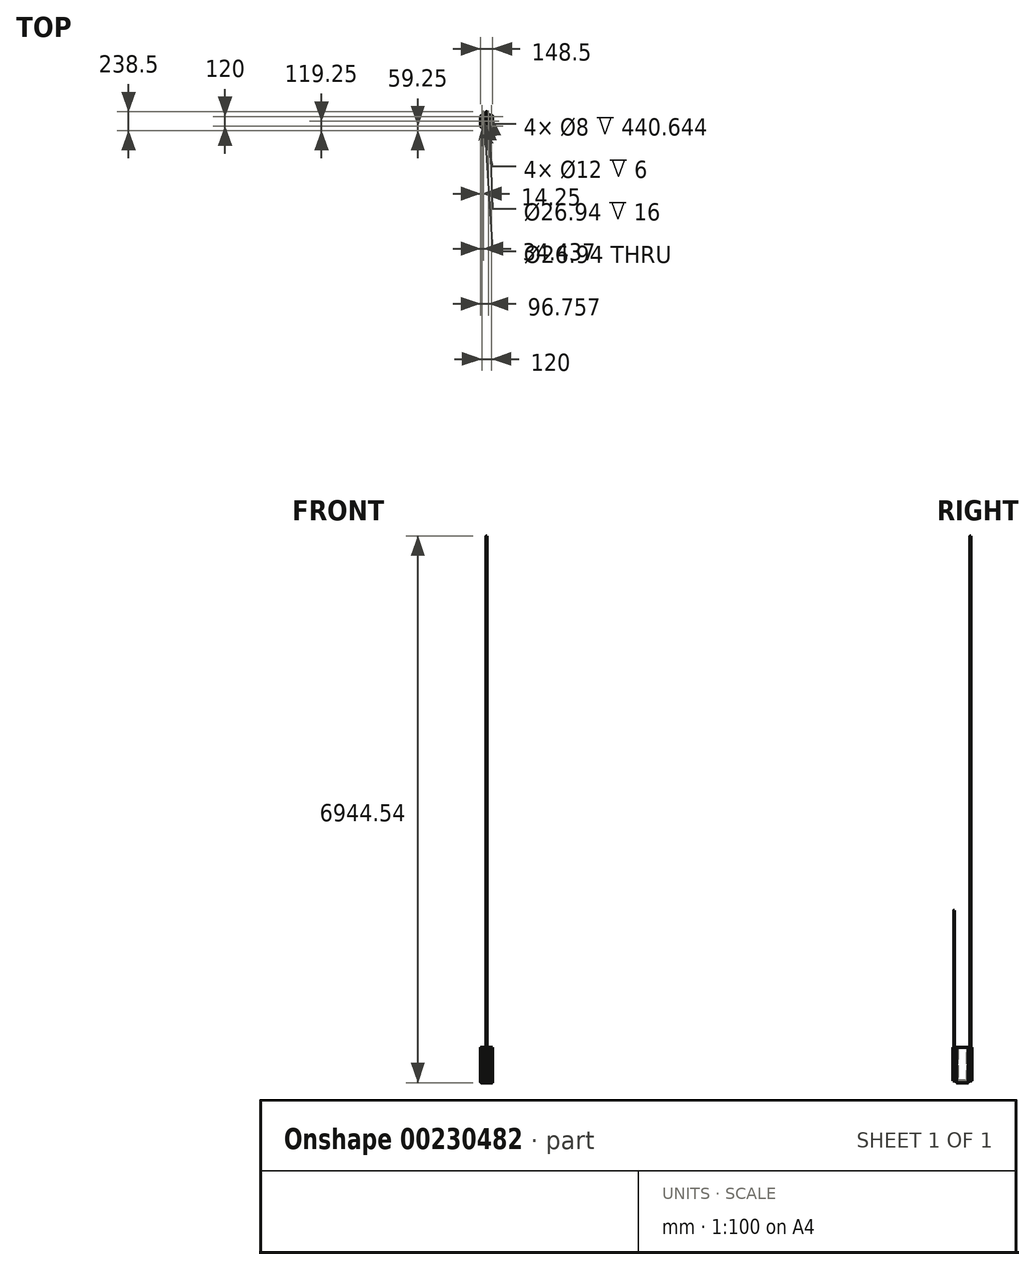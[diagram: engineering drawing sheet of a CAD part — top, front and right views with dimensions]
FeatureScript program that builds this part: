
annotation { "Feature Type Name" : "Feature", "Feature Type Description" : "" }
export const myFeature = defineFeature(function(context is Context, id is Id, definition is map)
    precondition{}
    {
        {
            var Q0;
            Q0=qCreatedBy(makeId("Top.planeOp"),FACE);
            var sketch = newSketch(context, id + "F0", { "sketchPlane" : qUnion([Q0])});
            skPoint(sketch, "E0.rect.middle", {"position": v(0, 0) * mm});
            skLineSegment(sketch, "E1.bottom", {"start": v(-64.25, -74.25) * mm, "end": v(64.25, -74.25) * mm});
            skLineSegment(sketch, "E1.top", {"start": v(-64.25, 74.25) * mm, "end": v(64.25, 74.25) * mm});
            skLineSegment(sketch, "E1.left", {"start": v(-74.25, -64.25) * mm, "end": v(-74.25, 64.25) * mm});
            skLineSegment(sketch, "E1.right", {"start": v(74.25, -64.25) * mm, "end": v(74.25, 64.25) * mm});
            skLineSegment(sketch, "E2", {"start": v(-74.25, 74.25) * mm, "end": v(74.25, -74.25) * mm, "construction": true});
            skLineSegment(sketch, "E3", {"start": v(74.25, 74.25) * mm, "end": v(-74.25, -74.25) * mm, "construction": true});
            skCircle(sketch, "E4", {"center": v(-60, 60) * mm, "radius": 4 * mm});
            skCircle(sketch, "E5", {"center": v(60, 60) * mm, "radius": 4 * mm});
            skCircle(sketch, "E6", {"center": v(60, -60) * mm, "radius": 4 * mm});
            skCircle(sketch, "E7", {"center": v(-60, -60) * mm, "radius": 4 * mm});
            skLineSegment(sketch, "E8", {"start": v(-60, 60) * mm, "end": v(60, 60) * mm, "construction": true});
            skLineSegment(sketch, "E9", {"start": v(60, 60) * mm, "end": v(60, -60) * mm, "construction": true});
            skLineSegment(sketch, "E10", {"start": v(60, -60) * mm, "end": v(-60, -60) * mm, "construction": true});
            skLineSegment(sketch, "E11", {"start": v(-60, -60) * mm, "end": v(-60, 60) * mm, "construction": true});
            skLineSegment(sketch, "E12", {"start": v(-60, 38.83) * mm, "end": v(-60, -38.83) * mm});
            skLineSegment(sketch, "E13", {"start": v(60, 38.83) * mm, "end": v(60, -38.83) * mm});
            skArc(sketch, "E14", {"start": v(54.26, 47.88) * mm, "mid": v(0, 60) * mm, "end": v(-54.26, 47.88) * mm});
            skArc(sketch, "E15", {"start": v(-54.26, -47.88) * mm, "mid": v(0, -60) * mm, "end": v(54.26, -47.88) * mm});
            skLineSegment(sketch, "E16", {"start": v(-60, 0) * mm, "end": v(60, 0) * mm, "construction": true});
            skPoint(sketch, "E17.visualSharp", {"position": v(-60, -45) * mm});
            skArc(sketch, "E17.filletArc", {"start": v(-60, -38.83) * mm, "mid": v(-58.44, -44.2) * mm, "end": v(-54.26, -47.88) * mm});
            skPoint(sketch, "E18.visualSharp", {"position": v(-60, 45) * mm});
            skArc(sketch, "E18.filletArc", {"start": v(-54.26, 47.88) * mm, "mid": v(-58.44, 44.2) * mm, "end": v(-60, 38.83) * mm});
            skPoint(sketch, "E19.visualSharp", {"position": v(60, 45) * mm});
            skArc(sketch, "E19.filletArc", {"start": v(60, 38.83) * mm, "mid": v(58.44, 44.2) * mm, "end": v(54.26, 47.88) * mm});
            skPoint(sketch, "E20.visualSharp", {"position": v(60, -45) * mm});
            skArc(sketch, "E20.filletArc", {"start": v(54.26, -47.88) * mm, "mid": v(58.44, -44.2) * mm, "end": v(60, -38.83) * mm});
            skPoint(sketch, "E21.visualSharp", {"position": v(-74.25, 74.25) * mm});
            skArc(sketch, "E21.filletArc", {"start": v(-64.25, 74.25) * mm, "mid": v(-71.32, 71.32) * mm, "end": v(-74.25, 64.25) * mm});
            skPoint(sketch, "E22.visualSharp", {"position": v(74.25, 74.25) * mm});
            skArc(sketch, "E22.filletArc", {"start": v(74.25, 64.25) * mm, "mid": v(71.32, 71.32) * mm, "end": v(64.25, 74.25) * mm});
            skPoint(sketch, "E23.visualSharp", {"position": v(74.25, -74.25) * mm});
            skArc(sketch, "E23.filletArc", {"start": v(64.25, -74.25) * mm, "mid": v(71.32, -71.32) * mm, "end": v(74.25, -64.25) * mm});
            skPoint(sketch, "E24.visualSharp", {"position": v(-74.25, -74.25) * mm});
            skArc(sketch, "E24.filletArc", {"start": v(-74.25, -64.25) * mm, "mid": v(-71.32, -71.32) * mm, "end": v(-64.25, -74.25) * mm});
            skArc(sketch, "E25.0", {"start": v(57, 38.83) * mm, "mid": v(55.9, 42.58) * mm, "end": v(52.98, 45.17) * mm});
            skLineSegment(sketch, "E25.1", {"start": v(57, 38.83) * mm, "end": v(57, -38.83) * mm});
            skArc(sketch, "E25.2", {"start": v(52.98, -45.17) * mm, "mid": v(55.9, -42.58) * mm, "end": v(57, -38.83) * mm});
            skArc(sketch, "E25.3", {"start": v(-52.98, -45.17) * mm, "mid": v(0, -57) * mm, "end": v(52.98, -45.17) * mm});
            skArc(sketch, "E25.4", {"start": v(-57, -38.83) * mm, "mid": v(-55.9, -42.58) * mm, "end": v(-52.98, -45.17) * mm});
            skArc(sketch, "E25.5", {"start": v(52.98, 45.17) * mm, "mid": v(0, 57) * mm, "end": v(-52.98, 45.17) * mm});
            skLineSegment(sketch, "E25.6", {"start": v(-57, 38.83) * mm, "end": v(-57, -38.83) * mm});
            skArc(sketch, "E25.7", {"start": v(-52.98, 45.17) * mm, "mid": v(-55.9, 42.58) * mm, "end": v(-57, 38.83) * mm});
            skArc(sketch, "E26.0", {"start": v(-55.96, 51.5) * mm, "mid": v(-61.82, 46.33) * mm, "end": v(-64, 38.83) * mm});
            skArc(sketch, "E26.1", {"start": v(55.96, 51.5) * mm, "mid": v(0, 64) * mm, "end": v(-55.96, 51.5) * mm});
            skArc(sketch, "E26.2", {"start": v(64, 38.83) * mm, "mid": v(61.82, 46.33) * mm, "end": v(55.96, 51.5) * mm});
            skLineSegment(sketch, "E26.3", {"start": v(64, 38.83) * mm, "end": v(64, -38.83) * mm});
            skArc(sketch, "E26.4", {"start": v(55.96, -51.5) * mm, "mid": v(61.82, -46.33) * mm, "end": v(64, -38.83) * mm});
            skLineSegment(sketch, "E26.5", {"start": v(-64, 38.83) * mm, "end": v(-64, -38.83) * mm});
            skArc(sketch, "E26.6", {"start": v(-55.96, -51.5) * mm, "mid": v(0, -64) * mm, "end": v(55.96, -51.5) * mm});
            skArc(sketch, "E26.7", {"start": v(-64, -38.83) * mm, "mid": v(-61.82, -46.33) * mm, "end": v(-55.96, -51.5) * mm});
            skSolve(sketch);
        }
        {
            var Q0;
            Q0=makeQuery(id+"F0.imprint","IMPRINT",FACE,{"disambiguationData":[TD([[makeQuery(id+"F0.imprint","IMPRINT",EDGE,{"derivedFrom":sQuery(id+"F0.wireOp",EDGE,"E1.bottom")}),1.0]])]});
            var Q1;
            Q1=makeQuery(id+"F0.imprint","IMPRINT",FACE,{"disambiguationData":[TD([[makeQuery(id+"F0.imprint","IMPRINT",EDGE,{"derivedFrom":sQuery(id+"F0.wireOp",EDGE,"E12")}),1.0]])]});
            var Q2;
            Q2=makeQuery(id+"F0.imprint","IMPRINT",FACE,{"disambiguationData":[TD([[makeQuery(id+"F0.imprint","IMPRINT",EDGE,{"derivedFrom":sQuery(id+"F0.wireOp",EDGE,"E25.0")}),1.0]])]});
            var Q3;
            Q3=makeQuery(id+"F0.imprint","IMPRINT",FACE,{"disambiguationData":[TD([[makeQuery(id+"F0.imprint","IMPRINT",EDGE,{"derivedFrom":sQuery(id+"F0.wireOp",EDGE,"E12")}),-1.0]])]});
            extrude(context, id + "F1", {"entities" : qUnion([Q0, Q1, Q2, Q3]), "oppositeDirection" : true, "depth" : 25 * mm});
        }
        {
            var Q0;
            Q0=makeQuery(id+"F0.imprint","IMPRINT",FACE,{"disambiguationData":[TD([[makeQuery(id+"F0.imprint","IMPRINT",EDGE,{"derivedFrom":sQuery(id+"F0.wireOp",EDGE,"E12")}),1.0]])]});
            extrude(context, id + "F2", {"entities" : qUnion([Q0]), "operationType" : NewBodyOperationType.ADD, "depth" : 3 * mm});
        }
        {
            var Q0;
            Q0=makeQuery(id+"F0.imprint","IMPRINT",FACE,{"disambiguationData":[TD([[makeQuery(id+"F0.imprint","IMPRINT",EDGE,{"derivedFrom":sQuery(id+"F0.wireOp",EDGE,"E25.0")}),1.0]])]});
            extrude(context, id + "F3", {"entities" : qUnion([Q0]), "operationType" : NewBodyOperationType.REMOVE, "oppositeDirection" : true, "depth" : 18 * mm});
        }
        {
            var Q0;
            Q0=makeQuery(id+"F2.opExtrude","CAP_FACE",FACE,{"disambiguationData":[OSD([sQuery(id+"F0.wireOp",EDGE,"E12"),sQuery(id+"F0.wireOp",EDGE,"E13"),sQuery(id+"F0.wireOp",EDGE,"E14"),sQuery(id+"F0.wireOp",EDGE,"E15"),sQuery(id+"F0.wireOp",EDGE,"E17.filletArc"),sQuery(id+"F0.wireOp",EDGE,"E18.filletArc"),sQuery(id+"F0.wireOp",EDGE,"E19.filletArc"),sQuery(id+"F0.wireOp",EDGE,"E20.filletArc"),sQuery(id+"F0.wireOp",EDGE,"E25.0"),sQuery(id+"F0.wireOp",EDGE,"E25.1"),sQuery(id+"F0.wireOp",EDGE,"E25.2"),sQuery(id+"F0.wireOp",EDGE,"E25.3"),sQuery(id+"F0.wireOp",EDGE,"E25.4"),sQuery(id+"F0.wireOp",EDGE,"E25.5"),sQuery(id+"F0.wireOp",EDGE,"E25.6"),sQuery(id+"F0.wireOp",EDGE,"E25.7")])],"isStart":false});
            var sketch = newSketch(context, id + "F4", { "sketchPlane" : qUnion([Q0])});
            skArc(sketch, "E27.0", {"start": v(-18.34, -40.45) * mm, "mid": v(0, -42) * mm, "end": v(18.34, -40.45) * mm});
            skArc(sketch, "E28.0", {"start": v(18.34, 40.45) * mm, "mid": v(0, 42) * mm, "end": v(-18.34, 40.45) * mm});
            skLineSegment(sketch, "E29", {"start": v(-25, 32.57) * mm, "end": v(-25, -32.57) * mm});
            skLineSegment(sketch, "E30", {"start": v(25, 32.57) * mm, "end": v(25, -32.57) * mm});
            skLineSegment(sketch, "E31", {"start": v(-25, 39.1) * mm, "end": v(25, 39.1) * mm, "construction": true});
            skLineSegment(sketch, "E32", {"start": v(-25, -39.1) * mm, "end": v(25, -39.1) * mm, "construction": true});
            skPoint(sketch, "E33.visualSharp", {"position": v(-25, 39.1) * mm});
            skArc(sketch, "E33.filletArc", {"start": v(-18.34, 40.45) * mm, "mid": v(-23.11, 37.73) * mm, "end": v(-25, 32.57) * mm});
            skPoint(sketch, "E34.visualSharp", {"position": v(25, 39.1) * mm});
            skArc(sketch, "E34.filletArc", {"start": v(25, 32.57) * mm, "mid": v(23.11, 37.73) * mm, "end": v(18.34, 40.45) * mm});
            skPoint(sketch, "E35.visualSharp", {"position": v(25, -39.1) * mm});
            skArc(sketch, "E35.filletArc", {"start": v(18.34, -40.45) * mm, "mid": v(23.11, -37.73) * mm, "end": v(25, -32.57) * mm});
            skPoint(sketch, "E36.visualSharp", {"position": v(-25, -39.1) * mm});
            skArc(sketch, "E36.filletArc", {"start": v(-25, -32.57) * mm, "mid": v(-23.11, -37.73) * mm, "end": v(-18.34, -40.45) * mm});
            skArc(sketch, "E37.0", {"start": v(52.98, 45.17) * mm, "mid": v(0, 57) * mm, "end": v(-52.98, 45.17) * mm});
            skArc(sketch, "E37.1", {"start": v(-52.98, 45.17) * mm, "mid": v(-55.9, 42.58) * mm, "end": v(-57, 38.83) * mm});
            skLineSegment(sketch, "E37.2", {"start": v(-57, 38.83) * mm, "end": v(-57, -38.83) * mm});
            skArc(sketch, "E37.3", {"start": v(-57, -38.83) * mm, "mid": v(-55.9, -42.58) * mm, "end": v(-52.98, -45.17) * mm});
            skArc(sketch, "E37.4", {"start": v(-52.98, -45.17) * mm, "mid": v(0, -57) * mm, "end": v(52.98, -45.17) * mm});
            skArc(sketch, "E37.5", {"start": v(52.98, -45.17) * mm, "mid": v(55.9, -42.58) * mm, "end": v(57, -38.83) * mm});
            skLineSegment(sketch, "E37.6", {"start": v(57, 38.83) * mm, "end": v(57, -38.83) * mm});
            skArc(sketch, "E37.7", {"start": v(57, 38.83) * mm, "mid": v(55.9, 42.58) * mm, "end": v(52.98, 45.17) * mm});
            skLineSegment(sketch, "E38.0", {"start": v(23, 32.57) * mm, "end": v(23, -32.57) * mm});
            skArc(sketch, "E38.1", {"start": v(18, -38.48) * mm, "mid": v(21.58, -36.44) * mm, "end": v(23, -32.57) * mm});
            skArc(sketch, "E38.2", {"start": v(-18, -38.48) * mm, "mid": v(0, -40) * mm, "end": v(18, -38.48) * mm});
            skArc(sketch, "E38.3", {"start": v(-23, -32.57) * mm, "mid": v(-21.58, -36.44) * mm, "end": v(-18, -38.48) * mm});
            skLineSegment(sketch, "E38.4", {"start": v(-23, 32.57) * mm, "end": v(-23, -32.57) * mm});
            skArc(sketch, "E38.5", {"start": v(23, 32.57) * mm, "mid": v(21.58, 36.44) * mm, "end": v(18, 38.48) * mm});
            skArc(sketch, "E38.6", {"start": v(-18, 38.48) * mm, "mid": v(-21.58, 36.44) * mm, "end": v(-23, 32.57) * mm});
            skArc(sketch, "E38.7", {"start": v(18, 38.48) * mm, "mid": v(0, 40) * mm, "end": v(-18, 38.48) * mm});
            skArc(sketch, "E39.0", {"start": v(21, 32.57) * mm, "mid": v(20.06, 35.15) * mm, "end": v(17.67, 36.5) * mm});
            skLineSegment(sketch, "E39.1", {"start": v(21, 32.57) * mm, "end": v(21, -32.57) * mm});
            skArc(sketch, "E39.2", {"start": v(17.67, -36.5) * mm, "mid": v(20.06, -35.15) * mm, "end": v(21, -32.57) * mm});
            skArc(sketch, "E39.3", {"start": v(-17.67, -36.5) * mm, "mid": v(0, -38) * mm, "end": v(17.67, -36.5) * mm});
            skArc(sketch, "E39.4", {"start": v(-21, -32.57) * mm, "mid": v(-20.06, -35.15) * mm, "end": v(-17.67, -36.5) * mm});
            skArc(sketch, "E39.5", {"start": v(17.67, 36.5) * mm, "mid": v(0, 38) * mm, "end": v(-17.67, 36.5) * mm});
            skLineSegment(sketch, "E39.6", {"start": v(-21, 32.57) * mm, "end": v(-21, -32.57) * mm});
            skArc(sketch, "E39.7", {"start": v(-17.67, 36.5) * mm, "mid": v(-20.06, 35.15) * mm, "end": v(-21, 32.57) * mm});
            skLineSegment(sketch, "E40", {"start": v(-25, 0) * mm, "end": v(25, 0) * mm, "construction": true});
            skLineSegment(sketch, "E41", {"start": v(-11, 5.5) * mm, "end": v(-11, 27.5) * mm});
            skLineSegment(sketch, "E42", {"start": v(-8, 30.5) * mm, "end": v(8, 30.5) * mm});
            skLineSegment(sketch, "E43", {"start": v(11, 27.5) * mm, "end": v(11, 13.5) * mm});
            skLineSegment(sketch, "E44", {"start": v(14, 10.5) * mm, "end": v(14, 10.5) * mm});
            skLineSegment(sketch, "E45", {"start": v(17, 7.5) * mm, "end": v(17, 5.5) * mm});
            skLineSegment(sketch, "E46", {"start": v(14, 2.5) * mm, "end": v(-8, 2.5) * mm});
            skPoint(sketch, "E47.visualSharp", {"position": v(-11, 30.5) * mm});
            skArc(sketch, "E47.filletArc", {"start": v(-8, 30.5) * mm, "mid": v(-10.12, 29.62) * mm, "end": v(-11, 27.5) * mm});
            skPoint(sketch, "E48.visualSharp", {"position": v(11, 30.5) * mm});
            skArc(sketch, "E48.filletArc", {"start": v(11, 27.5) * mm, "mid": v(10.12, 29.62) * mm, "end": v(8, 30.5) * mm});
            skPoint(sketch, "E49.visualSharp", {"position": v(11, 10.5) * mm});
            skArc(sketch, "E49.filletArc", {"start": v(11, 13.5) * mm, "mid": v(11.88, 11.38) * mm, "end": v(14, 10.5) * mm});
            skPoint(sketch, "E50.visualSharp", {"position": v(17, 10.5) * mm});
            skArc(sketch, "E50.filletArc", {"start": v(17, 7.5) * mm, "mid": v(16.12, 9.62) * mm, "end": v(14, 10.5) * mm});
            skPoint(sketch, "E51.visualSharp", {"position": v(17, 2.5) * mm});
            skArc(sketch, "E51.filletArc", {"start": v(14, 2.5) * mm, "mid": v(16.12, 3.38) * mm, "end": v(17, 5.5) * mm});
            skPoint(sketch, "E52.visualSharp", {"position": v(-11, 2.5) * mm});
            skArc(sketch, "E52.filletArc", {"start": v(-11, 5.5) * mm, "mid": v(-10.12, 3.38) * mm, "end": v(-8, 2.5) * mm});
            skLineSegment(sketch, "E53.0.MirrorCS", {"start": v(14, -2.5) * mm, "end": v(-8, -2.5) * mm});
            skArc(sketch, "E54.0.MirrorCS", {"start": v(-11, -5.5) * mm, "mid": v(-10.12, -3.38) * mm, "end": v(-8, -2.5) * mm});
            skLineSegment(sketch, "E55.0.MirrorCS", {"start": v(-11, -5.5) * mm, "end": v(-11, -27.5) * mm});
            skArc(sketch, "E56.0.MirrorCS", {"start": v(-8, -30.5) * mm, "mid": v(-10.12, -29.62) * mm, "end": v(-11, -27.5) * mm});
            skLineSegment(sketch, "E57.0.MirrorCS", {"start": v(-8, -30.5) * mm, "end": v(8, -30.5) * mm});
            skArc(sketch, "E58.0.MirrorCS", {"start": v(11, -27.5) * mm, "mid": v(10.12, -29.62) * mm, "end": v(8, -30.5) * mm});
            skLineSegment(sketch, "E59.0.MirrorCS", {"start": v(11, -27.5) * mm, "end": v(11, -13.5) * mm});
            skArc(sketch, "E60.0.MirrorCS", {"start": v(11, -13.5) * mm, "mid": v(11.88, -11.38) * mm, "end": v(14, -10.5) * mm});
            skArc(sketch, "E61.0.MirrorCS", {"start": v(17, -7.5) * mm, "mid": v(16.12, -9.62) * mm, "end": v(14, -10.5) * mm});
            skLineSegment(sketch, "E62.0.MirrorCS", {"start": v(17, -7.5) * mm, "end": v(17, -5.5) * mm});
            skArc(sketch, "E63.0.MirrorCS", {"start": v(14, -2.5) * mm, "mid": v(16.12, -3.38) * mm, "end": v(17, -5.5) * mm});
            skSolve(sketch);
        }
        {
            var Q0;
            Q0=makeQuery(id+"F4.imprint","IMPRINT",FACE,{"disambiguationData":[TD([[makeQuery(id+"F4.imprint","IMPRINT",EDGE,{"derivedFrom":sQuery(id+"F4.wireOp",EDGE,"E27.0")}),1.0]])]});
            var Q1;
            Q1=makeQuery(id+"F4.imprint","IMPRINT",FACE,{"disambiguationData":[TD([[makeQuery(id+"F4.imprint","IMPRINT",EDGE,{"derivedFrom":sQuery(id+"F4.wireOp",EDGE,"E38.0")}),-1.0]])]});
            var Q2;
            Q2=makeQuery(id+"F4.imprint","IMPRINT",FACE,{"disambiguationData":[TD([[makeQuery(id+"F4.imprint","IMPRINT",EDGE,{"derivedFrom":sQuery(id+"F4.wireOp",EDGE,"E39.0")}),1.0]])]});
            extrude(context, id + "F5", {"entities" : qUnion([Q0, Q1, Q2]), "operationType" : NewBodyOperationType.ADD, "endBound" : BoundingType.UP_TO_NEXT, "oppositeDirection" : true, "depth" : 25 * mm});
        }
        {
            var Q0;
            Q0=makeQuery(id+"F4.imprint","IMPRINT",FACE,{"disambiguationData":[TD([[makeQuery(id+"F4.imprint","IMPRINT",EDGE,{"derivedFrom":sQuery(id+"F4.wireOp",EDGE,"E38.0")}),-1.0]])]});
            extrude(context, id + "F6", {"entities" : qUnion([Q0]), "operationType" : NewBodyOperationType.REMOVE, "oppositeDirection" : true, "depth" : 2 * mm});
        }
        {
            var Q0;
            Q0=makeQuery(id+"F1.opExtrude","CAP_FACE",FACE,{"disambiguationData":[OSD([sQuery(id+"F0.wireOp",EDGE,"E1.bottom"),sQuery(id+"F0.wireOp",EDGE,"E1.top"),sQuery(id+"F0.wireOp",EDGE,"E1.left"),sQuery(id+"F0.wireOp",EDGE,"E1.right"),sQuery(id+"F0.wireOp",EDGE,"E4"),sQuery(id+"F0.wireOp",EDGE,"E5"),sQuery(id+"F0.wireOp",EDGE,"E6"),sQuery(id+"F0.wireOp",EDGE,"E7"),sQuery(id+"F0.wireOp",EDGE,"E21.filletArc"),sQuery(id+"F0.wireOp",EDGE,"E22.filletArc"),sQuery(id+"F0.wireOp",EDGE,"E23.filletArc"),sQuery(id+"F0.wireOp",EDGE,"E24.filletArc")])],"isStart":false});
            var sketch = newSketch(context, id + "F7", { "sketchPlane" : qUnion([Q0])});
            skCircle(sketch, "E64", {"center": v(22.5, 0) * mm, "radius": 13.47 * mm});
            skCircle(sketch, "E65", {"center": v(-39.81, 0) * mm, "radius": 13.47 * mm});
            skLineSegment(sketch, "E66", {"start": v(74.25, 0) * mm, "end": v(-74.25, 0) * mm});
            skCircle(sketch, "E67", {"center": v(22.5, 0) * mm, "radius": 18.47 * mm});
            skCircle(sketch, "E68", {"center": v(60, -60) * mm, "radius": 6 * mm});
            skCircle(sketch, "E69", {"center": v(-60, -60) * mm, "radius": 6 * mm});
            skCircle(sketch, "E70", {"center": v(-60, 60) * mm, "radius": 6 * mm});
            skCircle(sketch, "E71", {"center": v(60, 60) * mm, "radius": 6 * mm});
            skSolve(sketch);
        }
        {
            var Q0;
            {var subQ1=sQuery(id+"F7.wireOp",EDGE,"E66");var subQ4=sQuery(id+"F7.wireOp",EDGE,"E64");var subQ6=makeQuery(id+"F7.imprint","INTERSECT",VERTEX,{"disambiguationData":[OD(0.0)],"derivedFrom":[subQ4,subQ1]});Q0=makeQuery(id+"F7.imprint","IMPRINT",FACE,{"disambiguationData":[TD([[makeQuery(id+"F7.imprint","IMPRINT",EDGE,{"disambiguationData":[TD([[subQ6,-1.0]])],"derivedFrom":subQ4}),-1.0]])]});}
            var Q1;
            {var subQ0=sQuery(id+"F7.wireOp",EDGE,"E66");var subQ1=sQuery(id+"F7.wireOp",EDGE,"E64");var subQ3=makeQuery(id+"F7.imprint","INTERSECT",VERTEX,{"disambiguationData":[OD(0.0)],"derivedFrom":[subQ1,subQ0]});Q1=makeQuery(id+"F7.imprint","IMPRINT",FACE,{"disambiguationData":[TD([[makeQuery(id+"F7.imprint","IMPRINT",EDGE,{"disambiguationData":[TD([[subQ3,-1.0]])],"derivedFrom":subQ1}),1.0]])]});}
            var Q2;
            {var subQ0=sQuery(id+"F7.wireOp",EDGE,"E66");var subQ1=sQuery(id+"F7.wireOp",EDGE,"E64");var subQ3=makeQuery(id+"F7.imprint","INTERSECT",VERTEX,{"disambiguationData":[OD(0.0)],"derivedFrom":[subQ1,subQ0]});Q2=makeQuery(id+"F7.imprint","IMPRINT",FACE,{"disambiguationData":[TD([[makeQuery(id+"F7.imprint","IMPRINT",EDGE,{"disambiguationData":[TD([[subQ3,1.0]])],"derivedFrom":subQ1}),1.0]])]});}
            var Q3;
            {var subQ1=sQuery(id+"F7.wireOp",EDGE,"E66");var subQ4=sQuery(id+"F7.wireOp",EDGE,"E64");var subQ6=makeQuery(id+"F7.imprint","INTERSECT",VERTEX,{"disambiguationData":[OD(0.0)],"derivedFrom":[subQ4,subQ1]});Q3=makeQuery(id+"F7.imprint","IMPRINT",FACE,{"disambiguationData":[TD([[makeQuery(id+"F7.imprint","IMPRINT",EDGE,{"disambiguationData":[TD([[subQ6,1.0]])],"derivedFrom":subQ4}),-1.0]])]});}
            extrude(context, id + "F8", {"entities" : qUnion([Q0, Q1, Q2, Q3]), "operationType" : NewBodyOperationType.ADD, "oppositeDirection" : true, "depth" : 20 * mm});
        }
        {
            var Q0;
            {var subQ0=sQuery(id+"F7.wireOp",EDGE,"E66");var subQ1=sQuery(id+"F7.wireOp",EDGE,"E64");var subQ3=makeQuery(id+"F7.imprint","INTERSECT",VERTEX,{"disambiguationData":[OD(0.0)],"derivedFrom":[subQ1,subQ0]});Q0=makeQuery(id+"F7.imprint","IMPRINT",FACE,{"disambiguationData":[TD([[makeQuery(id+"F7.imprint","IMPRINT",EDGE,{"disambiguationData":[TD([[subQ3,-1.0]])],"derivedFrom":subQ1}),1.0]])]});}
            var Q1;
            {var subQ0=sQuery(id+"F7.wireOp",EDGE,"E66");var subQ1=sQuery(id+"F7.wireOp",EDGE,"E64");var subQ3=makeQuery(id+"F7.imprint","INTERSECT",VERTEX,{"disambiguationData":[OD(0.0)],"derivedFrom":[subQ1,subQ0]});Q1=makeQuery(id+"F7.imprint","IMPRINT",FACE,{"disambiguationData":[TD([[makeQuery(id+"F7.imprint","IMPRINT",EDGE,{"disambiguationData":[TD([[subQ3,1.0]])],"derivedFrom":subQ1}),1.0]])]});}
            extrude(context, id + "F9", {"entities" : qUnion([Q0, Q1]), "operationType" : NewBodyOperationType.REMOVE, "oppositeDirection" : true, "depth" : 16 * mm});
        }
        {
            var Q0;
            {var subQ0=sQuery(id+"F7.wireOp",EDGE,"E66");var subQ1=sQuery(id+"F7.wireOp",EDGE,"E65");var subQ3=makeQuery(id+"F7.imprint","INTERSECT",VERTEX,{"disambiguationData":[OD(0.0)],"derivedFrom":[subQ1,subQ0]});Q0=makeQuery(id+"F7.imprint","IMPRINT",FACE,{"disambiguationData":[TD([[makeQuery(id+"F7.imprint","IMPRINT",EDGE,{"disambiguationData":[TD([[subQ3,-1.0]])],"derivedFrom":subQ1}),1.0]])]});}
            var Q1;
            {var subQ0=sQuery(id+"F7.wireOp",EDGE,"E66");var subQ1=sQuery(id+"F7.wireOp",EDGE,"E65");var subQ3=makeQuery(id+"F7.imprint","INTERSECT",VERTEX,{"disambiguationData":[OD(0.0)],"derivedFrom":[subQ1,subQ0]});Q1=makeQuery(id+"F7.imprint","IMPRINT",FACE,{"disambiguationData":[TD([[makeQuery(id+"F7.imprint","IMPRINT",EDGE,{"disambiguationData":[TD([[subQ3,1.0]])],"derivedFrom":subQ1}),1.0]])]});}
            extrude(context, id + "F10", {"entities" : qUnion([Q0, Q1]), "operationType" : NewBodyOperationType.REMOVE, "oppositeDirection" : true, "depth" : 25 * mm});
        }
        {
            var Q0;
            Q0=makeQuery(id+"F7.imprint","IMPRINT",FACE,{"disambiguationData":[TD([[makeQuery(id+"F7.imprint","IMPRINT",EDGE,{"derivedFrom":sQuery(id+"F7.wireOp",EDGE,"E68")}),1.0]])]});
            var Q1;
            Q1=makeQuery(id+"F7.imprint","IMPRINT",FACE,{"disambiguationData":[TD([[makeQuery(id+"F7.imprint","IMPRINT",EDGE,{"derivedFrom":makeQuery(id+"F1.opExtrude","CAP_EDGE",EDGE,{"disambiguationData":[OSD([sQuery(id+"F0.wireOp",EDGE,"E5")])],"isStart":false})}),-1.0]])]});
            var Q2;
            Q2=makeQuery(id+"F7.imprint","IMPRINT",FACE,{"disambiguationData":[TD([[makeQuery(id+"F7.imprint","IMPRINT",EDGE,{"derivedFrom":sQuery(id+"F7.wireOp",EDGE,"E69")}),1.0]])]});
            var Q3;
            Q3=makeQuery(id+"F7.imprint","IMPRINT",FACE,{"disambiguationData":[TD([[makeQuery(id+"F7.imprint","IMPRINT",EDGE,{"derivedFrom":makeQuery(id+"F1.opExtrude","CAP_EDGE",EDGE,{"disambiguationData":[OSD([sQuery(id+"F0.wireOp",EDGE,"E4")])],"isStart":false})}),-1.0]])]});
            var Q4;
            Q4=makeQuery(id+"F7.imprint","IMPRINT",FACE,{"disambiguationData":[TD([[makeQuery(id+"F7.imprint","IMPRINT",EDGE,{"derivedFrom":sQuery(id+"F7.wireOp",EDGE,"E70")}),1.0]])]});
            var Q5;
            Q5=makeQuery(id+"F7.imprint","IMPRINT",FACE,{"disambiguationData":[TD([[makeQuery(id+"F7.imprint","IMPRINT",EDGE,{"derivedFrom":makeQuery(id+"F1.opExtrude","CAP_EDGE",EDGE,{"disambiguationData":[OSD([sQuery(id+"F0.wireOp",EDGE,"E7")])],"isStart":false})}),-1.0]])]});
            var Q6;
            Q6=makeQuery(id+"F7.imprint","IMPRINT",FACE,{"disambiguationData":[TD([[makeQuery(id+"F7.imprint","IMPRINT",EDGE,{"derivedFrom":sQuery(id+"F7.wireOp",EDGE,"E71")}),1.0]])]});
            var Q7;
            Q7=makeQuery(id+"F7.imprint","IMPRINT",FACE,{"disambiguationData":[TD([[makeQuery(id+"F7.imprint","IMPRINT",EDGE,{"derivedFrom":makeQuery(id+"F1.opExtrude","CAP_EDGE",EDGE,{"disambiguationData":[OSD([sQuery(id+"F0.wireOp",EDGE,"E6")])],"isStart":false})}),-1.0]])]});
            extrude(context, id + "F11", {"entities" : qUnion([Q0, Q1, Q2, Q3, Q4, Q5, Q6, Q7]), "operationType" : NewBodyOperationType.REMOVE, "oppositeDirection" : true, "depth" : 6 * mm});
        }
        {
            var Q0;
            Q0=makeQuery(id+"F9.boolean.opBoolean","COPY",FACE,{"derivedFrom":makeQuery(id+"F9.opExtrude","CAP_FACE",FACE,{"disambiguationData":[OSD([sQuery(id+"F7.wireOp",EDGE,"E64")])],"isStart":false})});
            var sketch = newSketch(context, id + "F12", { "sketchPlane" : qUnion([Q0])});
            skArc(sketch, "E72.0", {"start": v(11, 14.45) * mm, "mid": v(6.45, 9.13) * mm, "end": v(4.2, 2.5) * mm});
            skArc(sketch, "E72.1", {"start": v(4.2, -2.5) * mm, "mid": v(6.45, -9.13) * mm, "end": v(11, -14.45) * mm});
            skLineSegment(sketch, "E73", {"start": v(4.2, -2.5) * mm, "end": v(14, -2.5) * mm});
            skLineSegment(sketch, "E74.0", {"start": v(14, 2.5) * mm, "end": v(4.2, 2.5) * mm});
            skArc(sketch, "E74.1", {"start": v(14, 2.5) * mm, "mid": v(16.12, 3.38) * mm, "end": v(17, 5.5) * mm});
            skLineSegment(sketch, "E74.2", {"start": v(17, 7.5) * mm, "end": v(17, 5.5) * mm});
            skArc(sketch, "E74.3", {"start": v(17, 7.5) * mm, "mid": v(16.12, 9.62) * mm, "end": v(14, 10.5) * mm});
            skArc(sketch, "E74.4", {"start": v(11, 13.5) * mm, "mid": v(11.88, 11.38) * mm, "end": v(14, 10.5) * mm});
            skLineSegment(sketch, "E74.5", {"start": v(11, 14.45) * mm, "end": v(11, 13.5) * mm});
            skLineSegment(sketch, "E74.7", {"start": v(14, -2.5) * mm, "end": v(4.2, -2.5) * mm});
            skArc(sketch, "E74.8", {"start": v(14, -2.5) * mm, "mid": v(16.12, -3.38) * mm, "end": v(17, -5.5) * mm});
            skLineSegment(sketch, "E74.9", {"start": v(17, -7.5) * mm, "end": v(17, -5.5) * mm});
            skArc(sketch, "E74.10", {"start": v(17, -7.5) * mm, "mid": v(16.12, -9.62) * mm, "end": v(14, -10.5) * mm});
            skArc(sketch, "E74.11", {"start": v(11, -13.5) * mm, "mid": v(11.88, -11.38) * mm, "end": v(14, -10.5) * mm});
            skLineSegment(sketch, "E74.12", {"start": v(11, -14.45) * mm, "end": v(11, -13.5) * mm});
            skPoint(sketch, "E75.orphan", {"position": v(11, -27.5) * mm});
            skPoint(sketch, "E76.orphan", {"position": v(-8, -2.5) * mm});
            skPoint(sketch, "E77.orphan", {"position": v(-8, 2.5) * mm});
            skPoint(sketch, "E78.orphan", {"position": v(11, 27.5) * mm});
            skSolve(sketch);
        }
        {
            var Q0;
            {var subQ7=sQuery(id+"F12.wireOp",EDGE,"E72.0");var subQ14=sQuery(id+"F12.wireOp",EDGE,"E72.1");var subQ16=sQuery(id+"F12.wireOp",EDGE,"E74.1");var subQ18=sQuery(id+"F12.wireOp",EDGE,"E74.8");Q0=qUnion([makeQuery(id+"F12.imprint","IMPRINT",FACE,{"disambiguationData":[TD([[makeQuery(id+"F12.imprint","IMPRINT",EDGE,{"derivedFrom":subQ7}),1.0]])]}),makeQuery(id+"F12.imprint","IMPRINT",FACE,{"disambiguationData":[TD([[makeQuery(id+"F12.imprint","IMPRINT",EDGE,{"derivedFrom":subQ14}),1.0]])]}),makeQuery(id+"F12.imprint","IMPRINT",FACE,{"disambiguationData":[TD([[makeQuery(id+"F12.imprint","IMPRINT",EDGE,{"derivedFrom":subQ16}),1.0]])]}),makeQuery(id+"F12.imprint","IMPRINT",FACE,{"disambiguationData":[TD([[makeQuery(id+"F12.imprint","IMPRINT",EDGE,{"derivedFrom":subQ18}),-1.0]])]})]);}
            var Q1;
            Q1=makeQuery(id+"F5.boolean.opBoolean","SPLIT",FACE,{"disambiguationData":[TD([makeQuery(id+"F5.opExtrude","SWEPT_FACE",FACE,{"disambiguationData":[OSD([sQuery(id+"F4.wireOp",EDGE,"E41")])]})])],"derivedFrom":makeQuery(id+"F3.boolean.opBoolean","COPY",FACE,{"derivedFrom":makeQuery(id+"F3.opExtrude","CAP_FACE",FACE,{"disambiguationData":[OSD([sQuery(id+"F0.wireOp",EDGE,"E25.0"),sQuery(id+"F0.wireOp",EDGE,"E25.1"),sQuery(id+"F0.wireOp",EDGE,"E25.2"),sQuery(id+"F0.wireOp",EDGE,"E25.3"),sQuery(id+"F0.wireOp",EDGE,"E25.4"),sQuery(id+"F0.wireOp",EDGE,"E25.5"),sQuery(id+"F0.wireOp",EDGE,"E25.6"),sQuery(id+"F0.wireOp",EDGE,"E25.7")])],"isStart":false})})});
            extrude(context, id + "F13", {"entities" : qUnion([Q0]), "operationType" : NewBodyOperationType.REMOVE, "endBound" : BoundingType.UP_TO_SURFACE, "endBoundEntityFace" : qUnion([Q1]), "depth" : 25 * mm});
        }
        {
            var Q0;
            Q0=makeQuery(id+"F3.boolean.opBoolean","COPY",EDGE,{"derivedFrom":makeQuery(id+"F3.opExtrude","CAP_EDGE",EDGE,{"disambiguationData":[OSD([sQuery(id+"F0.wireOp",EDGE,"E25.6")])],"isStart":false})});
            var Q1;
            Q1=makeQuery(id+"F8.boolean.opBoolean","INTERSECT",EDGE,{"derivedFrom":[makeQuery(id+"F5.opExtrude","SWEPT_FACE",FACE,{"disambiguationData":[OSD([sQuery(id+"F4.wireOp",EDGE,"E30")])]}),makeQuery(id+"F8.opExtrude","CAP_FACE",FACE,{"disambiguationData":[OSD([sQuery(id+"F7.wireOp",EDGE,"E67")])],"isStart":false})]});
            var Q2;
            Q2=makeQuery(id+"F8.boolean.opBoolean","INTERSECT",EDGE,{"disambiguationData":[OD(1.0)],"derivedFrom":[makeQuery(id+"F5.opExtrude","SWEPT_FACE",FACE,{"disambiguationData":[OSD([sQuery(id+"F4.wireOp",EDGE,"E30")])]}),makeQuery(id+"F8.opExtrude","SWEPT_FACE",FACE,{"disambiguationData":[OSD([sQuery(id+"F7.wireOp",EDGE,"E67")])]})]});
            var Q3;
            {var subQ0=sQuery(id+"F4.wireOp",EDGE,"E30");Q3=makeQuery(id+"F8.boolean.opBoolean","SPLIT",EDGE,{"disambiguationData":[TD([makeQuery(id+"F5.opExtrude","SWEPT_FACE",FACE,{"disambiguationData":[OSD([sQuery(id+"F4.wireOp",EDGE,"E35.filletArc")])]})])],"derivedFrom":makeQuery(id+"F5.opExtrude","CAP_EDGE",EDGE,{"disambiguationData":[OSD([subQ0])],"isStart":false})});}
            var Q4;
            {var subQ0=sQuery(id+"F0.wireOp",EDGE,"E25.7");var subQ1=sQuery(id+"F0.wireOp",EDGE,"E25.1");var subQ2=sQuery(id+"F0.wireOp",EDGE,"E25.6");var subQ3=sQuery(id+"F0.wireOp",EDGE,"E25.5");var subQ4=sQuery(id+"F0.wireOp",EDGE,"E25.4");var subQ5=sQuery(id+"F0.wireOp",EDGE,"E25.0");var subQ6=sQuery(id+"F0.wireOp",EDGE,"E25.2");var subQ7=sQuery(id+"F0.wireOp",EDGE,"E25.3");Q4=makeQuery(id+"F8.boolean.opBoolean","INTERSECT",EDGE,{"derivedFrom":[makeQuery(id+"F5.boolean.opBoolean","SPLIT",FACE,{"disambiguationData":[TD([makeQuery(id+"F2.opExtrude","SWEPT_FACE",FACE,{"disambiguationData":[OSD([subQ5])]})])],"derivedFrom":makeQuery(id+"F3.boolean.opBoolean","COPY",FACE,{"derivedFrom":makeQuery(id+"F3.opExtrude","CAP_FACE",FACE,{"disambiguationData":[OSD([subQ5,subQ1,subQ6,subQ7,subQ4,subQ3,subQ2,subQ0])],"isStart":false})})}),makeQuery(id+"F8.opExtrude","SWEPT_FACE",FACE,{"disambiguationData":[OSD([sQuery(id+"F7.wireOp",EDGE,"E67")])]})]});}
            var Q5;
            Q5=makeQuery(id+"F8.boolean.opBoolean","INTERSECT",EDGE,{"disambiguationData":[OD(0.0)],"derivedFrom":[makeQuery(id+"F5.opExtrude","SWEPT_FACE",FACE,{"disambiguationData":[OSD([sQuery(id+"F4.wireOp",EDGE,"E30")])]}),makeQuery(id+"F8.opExtrude","SWEPT_FACE",FACE,{"disambiguationData":[OSD([sQuery(id+"F7.wireOp",EDGE,"E67")])]})]});
            fillet(context, id + "F14", {"entities" : qUnion([Q0, Q1, Q2, Q3, Q4, Q5]), "radius" : 3 * mm, "tangentPropagation" : true, "allowEdgeOverflow" : false});
        }
        {
            var Q0;
            Q0=makeQuery(id+"F1.opExtrude","CAP_EDGE",EDGE,{"disambiguationData":[OSD([sQuery(id+"F0.wireOp",EDGE,"E1.bottom")])],"isStart":false});
            fillet(context, id + "F15", {"entities" : qUnion([Q0]), "radius" : 2 * mm, "tangentPropagation" : true, "allowEdgeOverflow" : false});
        }
        {
            var Q0;
            {var subQ0=sQuery(id+"F0.wireOp",EDGE,"E22.filletArc");var subQ1=sQuery(id+"F0.wireOp",EDGE,"E7");var subQ2=sQuery(id+"F0.wireOp",EDGE,"E6");var subQ3=sQuery(id+"F0.wireOp",EDGE,"E5");var subQ4=sQuery(id+"F0.wireOp",EDGE,"E4");var subQ5=sQuery(id+"F0.wireOp",EDGE,"E1.bottom");var subQ6=sQuery(id+"F0.wireOp",EDGE,"E21.filletArc");var subQ7=sQuery(id+"F0.wireOp",EDGE,"E1.top");var subQ8=sQuery(id+"F0.wireOp",EDGE,"E1.left");var subQ9=sQuery(id+"F0.wireOp",EDGE,"E1.right");var subQ10=sQuery(id+"F0.wireOp",EDGE,"E23.filletArc");var subQ11=sQuery(id+"F0.wireOp",EDGE,"E24.filletArc");Q0=makeQuery(id+"F2.boolean.opBoolean","SPLIT",FACE,{"disambiguationData":[TD([makeQuery(id+"F1.opExtrude","SWEPT_FACE",FACE,{"disambiguationData":[OSD([subQ5])]})])],"derivedFrom":makeQuery(id+"F1.opExtrude","CAP_FACE",FACE,{"disambiguationData":[OSD([subQ5,subQ7,subQ8,subQ9,subQ4,subQ3,subQ2,subQ1,subQ6,subQ0,subQ10,subQ11])],"isStart":true})});}
            var sketch = newSketch(context, id + "F16", { "sketchPlane" : qUnion([Q0])});
            skLineSegment(sketch, "E79", {"start": v(0, 74.25) * mm, "end": v(0, 104.25) * mm});
            skCircle(sketch, "E80", {"center": v(0, 104.25) * mm, "radius": 6 * mm});
            skArc(sketch, "E81", {"start": v(0, 119.25) * mm, "mid": v(-10.6, 114.86) * mm, "end": v(-15, 104.25) * mm});
            skArc(sketch, "E82", {"start": v(0, 119.25) * mm, "mid": v(10.6, 114.86) * mm, "end": v(15, 104.25) * mm});
            skLineSegment(sketch, "E83", {"start": v(-15, 104.25) * mm, "end": v(-15, 92.25) * mm});
            skLineSegment(sketch, "E84", {"start": v(-15, 92.25) * mm, "end": v(-33, 74.25) * mm});
            skLineSegment(sketch, "E85", {"start": v(15, 104.25) * mm, "end": v(15, 92.25) * mm});
            skLineSegment(sketch, "E86", {"start": v(15, 92.25) * mm, "end": v(33, 74.25) * mm});
            skLineSegment(sketch, "E87", {"start": v(-74.25, 0) * mm, "end": v(74.25, 0) * mm, "construction": true});
            skLineSegment(sketch, "E88.MirrorCS", {"start": v(-15, -92.25) * mm, "end": v(-33, -74.25) * mm});
            skLineSegment(sketch, "E89.MirrorCS", {"start": v(-15, -104.25) * mm, "end": v(-15, -92.25) * mm});
            skArc(sketch, "E90.MirrorCS", {"start": v(0, -119.25) * mm, "mid": v(-10.6, -114.86) * mm, "end": v(-15, -104.25) * mm});
            skArc(sketch, "E91.MirrorCS", {"start": v(0, -119.25) * mm, "mid": v(10.6, -114.86) * mm, "end": v(15, -104.25) * mm});
            skLineSegment(sketch, "E92.MirrorCS", {"start": v(15, -104.25) * mm, "end": v(15, -92.25) * mm});
            skLineSegment(sketch, "E93.MirrorCS", {"start": v(15, -92.25) * mm, "end": v(33, -74.25) * mm});
            skCircle(sketch, "E94.MirrorC", {"center": v(0, -104.25) * mm, "radius": 6 * mm});
            skLineSegment(sketch, "E95.MirrorCS", {"start": v(0, -74.25) * mm, "end": v(0, -104.25) * mm});
            skSolve(sketch);
        }
        {
            var Q0;
            Q0 = qSketchRegion(id + "F16", true);
            var Q1;
            {var subQ0=sQuery(id+"F16.wireOp",EDGE,"E88.MirrorCS");Q1=makeQuery(id+"F16.imprint","IMPRINT",FACE,{"disambiguationData":[TD([[makeQuery(id+"F16.imprint","IMPRINT",EDGE,{"derivedFrom":subQ0}),-1.0]])]});}
            var Q2;
            Q2=makeQuery(id+"F16.imprint","IMPRINT",FACE,{"disambiguationData":[TD([[makeQuery(id+"F16.imprint","IMPRINT",EDGE,{"derivedFrom":sQuery(id+"F16.wireOp",EDGE,"E80")}),-1.0]])]});
            var Q3;
            Q3=makeQuery(id+"F16.imprint","IMPRINT",FACE,{"disambiguationData":[TD([[makeQuery(id+"F16.imprint","IMPRINT",EDGE,{"derivedFrom":makeQuery(id+"F1.opExtrude","CAP_EDGE",EDGE,{"disambiguationData":[OSD([sQuery(id+"F0.wireOp",EDGE,"E1.left")])],"isStart":true})}),-1.0]])]});
            var Q4;
            Q4=makeQuery(id+"F2.opExtrude","CAP_FACE",FACE,{"disambiguationData":[OSD([sQuery(id+"F0.wireOp",EDGE,"E12"),sQuery(id+"F0.wireOp",EDGE,"E13"),sQuery(id+"F0.wireOp",EDGE,"E14"),sQuery(id+"F0.wireOp",EDGE,"E15"),sQuery(id+"F0.wireOp",EDGE,"E17.filletArc"),sQuery(id+"F0.wireOp",EDGE,"E18.filletArc"),sQuery(id+"F0.wireOp",EDGE,"E19.filletArc"),sQuery(id+"F0.wireOp",EDGE,"E20.filletArc"),sQuery(id+"F0.wireOp",EDGE,"E25.0"),sQuery(id+"F0.wireOp",EDGE,"E25.1"),sQuery(id+"F0.wireOp",EDGE,"E25.2"),sQuery(id+"F0.wireOp",EDGE,"E25.3"),sQuery(id+"F0.wireOp",EDGE,"E25.4"),sQuery(id+"F0.wireOp",EDGE,"E25.5"),sQuery(id+"F0.wireOp",EDGE,"E25.6"),sQuery(id+"F0.wireOp",EDGE,"E25.7")])],"isStart":false});
            extrude(context, id + "F17", {"entities" : qUnion([Q0, Q1, Q2, Q3]), "operationType" : NewBodyOperationType.ADD, "endBound" : BoundingType.UP_TO_SURFACE, "endBoundEntityFace" : qUnion([Q4]), "depth" : 25 * mm});
        }
        {
            var Q0;
            {var subQ0=sQuery(id+"F0.wireOp",EDGE,"E20.filletArc");var subQ1=sQuery(id+"F0.wireOp",EDGE,"E19.filletArc");var subQ2=sQuery(id+"F0.wireOp",EDGE,"E18.filletArc");var subQ3=sQuery(id+"F0.wireOp",EDGE,"E17.filletArc");var subQ4=sQuery(id+"F0.wireOp",EDGE,"E15");var subQ5=sQuery(id+"F0.wireOp",EDGE,"E14");var subQ6=sQuery(id+"F0.wireOp",EDGE,"E13");var subQ7=sQuery(id+"F0.wireOp",EDGE,"E12");Q0=makeQuery(id+"F17.boolean.opBoolean","MERGE",FACE,{"derivedFrom":[makeQuery(id+"F2.opExtrude","CAP_FACE",FACE,{"disambiguationData":[OSD([subQ7,subQ6,subQ5,subQ4,subQ3,subQ2,subQ1,subQ0,sQuery(id+"F0.wireOp",EDGE,"E25.0"),sQuery(id+"F0.wireOp",EDGE,"E25.1"),sQuery(id+"F0.wireOp",EDGE,"E25.2"),sQuery(id+"F0.wireOp",EDGE,"E25.3"),sQuery(id+"F0.wireOp",EDGE,"E25.4"),sQuery(id+"F0.wireOp",EDGE,"E25.5"),sQuery(id+"F0.wireOp",EDGE,"E25.6"),sQuery(id+"F0.wireOp",EDGE,"E25.7")])],"isStart":false}),makeQuery(id+"F17.opExtrude","CAP_FACE",FACE,{"disambiguationData":[OSD([sQuery(id+"F0.wireOp",EDGE,"E1.bottom"),sQuery(id+"F0.wireOp",EDGE,"E1.top"),sQuery(id+"F0.wireOp",EDGE,"E1.left"),sQuery(id+"F0.wireOp",EDGE,"E1.right"),sQuery(id+"F0.wireOp",EDGE,"E4"),sQuery(id+"F0.wireOp",EDGE,"E5"),sQuery(id+"F0.wireOp",EDGE,"E6"),sQuery(id+"F0.wireOp",EDGE,"E7"),subQ7,subQ6,subQ5,subQ4,subQ3,subQ2,subQ1,subQ0,sQuery(id+"F0.wireOp",EDGE,"E21.filletArc"),sQuery(id+"F0.wireOp",EDGE,"E22.filletArc"),sQuery(id+"F0.wireOp",EDGE,"E23.filletArc"),sQuery(id+"F0.wireOp",EDGE,"E24.filletArc"),sQuery(id+"F16.wireOp",EDGE,"E81"),sQuery(id+"F16.wireOp",EDGE,"E82"),sQuery(id+"F16.wireOp",EDGE,"E83"),sQuery(id+"F16.wireOp",EDGE,"E84"),sQuery(id+"F16.wireOp",EDGE,"E85"),sQuery(id+"F16.wireOp",EDGE,"E86"),sQuery(id+"F16.wireOp",EDGE,"E88.MirrorCS"),sQuery(id+"F16.wireOp",EDGE,"E89.MirrorCS"),sQuery(id+"F16.wireOp",EDGE,"E90.MirrorCS"),sQuery(id+"F16.wireOp",EDGE,"E91.MirrorCS"),sQuery(id+"F16.wireOp",EDGE,"E92.MirrorCS"),sQuery(id+"F16.wireOp",EDGE,"E93.MirrorCS")])],"isStart":false})]});}
            var sketch = newSketch(context, id + "F18", { "sketchPlane" : qUnion([Q0])});
            skCircle(sketch, "E96", {"center": v(0, 104.25) * mm, "radius": 6 * mm});
            skCircle(sketch, "E97", {"center": v(0, -104.25) * mm, "radius": 6 * mm});
            skSolve(sketch);
        }
        {
            var Q0;
            Q0=makeQuery(id+"F18.imprint","IMPRINT",FACE,{"disambiguationData":[TD([[makeQuery(id+"F18.imprint","IMPRINT",EDGE,{"derivedFrom":sQuery(id+"F18.wireOp",EDGE,"E96")}),1.0]])]});
            extrude(context, id + "F19", {"entities" : qUnion([Q0]), "operationType" : NewBodyOperationType.ADD, "endBound" : BoundingType.THROUGH_ALL, "depth" : 25 * mm});
        }
        {
            var Q0;
            {var subQ0=sQuery(id+"F0.wireOp",EDGE,"E20.filletArc");var subQ1=sQuery(id+"F0.wireOp",EDGE,"E19.filletArc");var subQ2=sQuery(id+"F0.wireOp",EDGE,"E18.filletArc");var subQ3=sQuery(id+"F0.wireOp",EDGE,"E17.filletArc");var subQ4=sQuery(id+"F0.wireOp",EDGE,"E15");var subQ5=sQuery(id+"F0.wireOp",EDGE,"E14");var subQ6=sQuery(id+"F0.wireOp",EDGE,"E13");var subQ7=sQuery(id+"F0.wireOp",EDGE,"E12");Q0=makeQuery(id+"F17.boolean.opBoolean","MERGE",FACE,{"derivedFrom":[makeQuery(id+"F2.opExtrude","CAP_FACE",FACE,{"disambiguationData":[OSD([subQ7,subQ6,subQ5,subQ4,subQ3,subQ2,subQ1,subQ0,sQuery(id+"F0.wireOp",EDGE,"E25.0"),sQuery(id+"F0.wireOp",EDGE,"E25.1"),sQuery(id+"F0.wireOp",EDGE,"E25.2"),sQuery(id+"F0.wireOp",EDGE,"E25.3"),sQuery(id+"F0.wireOp",EDGE,"E25.4"),sQuery(id+"F0.wireOp",EDGE,"E25.5"),sQuery(id+"F0.wireOp",EDGE,"E25.6"),sQuery(id+"F0.wireOp",EDGE,"E25.7")])],"isStart":false}),makeQuery(id+"F17.opExtrude","CAP_FACE",FACE,{"disambiguationData":[OSD([sQuery(id+"F0.wireOp",EDGE,"E1.bottom"),sQuery(id+"F0.wireOp",EDGE,"E1.top"),sQuery(id+"F0.wireOp",EDGE,"E1.left"),sQuery(id+"F0.wireOp",EDGE,"E1.right"),sQuery(id+"F0.wireOp",EDGE,"E4"),sQuery(id+"F0.wireOp",EDGE,"E5"),sQuery(id+"F0.wireOp",EDGE,"E6"),sQuery(id+"F0.wireOp",EDGE,"E7"),subQ7,subQ6,subQ5,subQ4,subQ3,subQ2,subQ1,subQ0,sQuery(id+"F0.wireOp",EDGE,"E21.filletArc"),sQuery(id+"F0.wireOp",EDGE,"E22.filletArc"),sQuery(id+"F0.wireOp",EDGE,"E23.filletArc"),sQuery(id+"F0.wireOp",EDGE,"E24.filletArc"),sQuery(id+"F16.wireOp",EDGE,"E81"),sQuery(id+"F16.wireOp",EDGE,"E82"),sQuery(id+"F16.wireOp",EDGE,"E83"),sQuery(id+"F16.wireOp",EDGE,"E84"),sQuery(id+"F16.wireOp",EDGE,"E85"),sQuery(id+"F16.wireOp",EDGE,"E86"),sQuery(id+"F16.wireOp",EDGE,"E88.MirrorCS"),sQuery(id+"F16.wireOp",EDGE,"E89.MirrorCS"),sQuery(id+"F16.wireOp",EDGE,"E90.MirrorCS"),sQuery(id+"F16.wireOp",EDGE,"E91.MirrorCS"),sQuery(id+"F16.wireOp",EDGE,"E92.MirrorCS"),sQuery(id+"F16.wireOp",EDGE,"E93.MirrorCS")])],"isStart":false})]});}
            extrude(context, id + "F20", {"entities" : qUnion([Q0]), "operationType" : NewBodyOperationType.ADD, "endBound" : BoundingType.THROUGH_ALL, "depth" : 25 * mm});
        }
        {
            var Q0;
            Q0=makeQuery(id+"F19.opExtrude","CAP_FACE",FACE,{"disambiguationData":[OSD([sQuery(id+"F18.wireOp",EDGE,"E96")])],"isStart":false});
            extrude(context, id + "F21", {"entities" : qUnion([Q0]), "operationType" : NewBodyOperationType.ADD, "endBound" : BoundingType.THROUGH_ALL, "depth" : 25 * mm});
        }
        {
            var Q0;
            Q0=makeQuery(id+"F21.opExtrude","CAP_FACE",FACE,{"disambiguationData":[OSD([sQuery(id+"F18.wireOp",EDGE,"E96")])],"isStart":false});
            extrude(context, id + "F22", {"entities" : qUnion([Q0]), "operationType" : NewBodyOperationType.ADD, "endBound" : BoundingType.THROUGH_ALL, "depth" : 25 * mm});
        }
        {
            var Q0;
            Q0=makeQuery(id+"F20.opExtrude","CAP_FACE",FACE,{"disambiguationData":[OSD([sQuery(id+"F0.wireOp",EDGE,"E12"),sQuery(id+"F0.wireOp",EDGE,"E13"),sQuery(id+"F0.wireOp",EDGE,"E14"),sQuery(id+"F0.wireOp",EDGE,"E15"),sQuery(id+"F0.wireOp",EDGE,"E17.filletArc"),sQuery(id+"F0.wireOp",EDGE,"E18.filletArc"),sQuery(id+"F0.wireOp",EDGE,"E19.filletArc"),sQuery(id+"F0.wireOp",EDGE,"E20.filletArc"),sQuery(id+"F0.wireOp",EDGE,"E25.0"),sQuery(id+"F0.wireOp",EDGE,"E25.1"),sQuery(id+"F0.wireOp",EDGE,"E25.2"),sQuery(id+"F0.wireOp",EDGE,"E25.3"),sQuery(id+"F0.wireOp",EDGE,"E25.4"),sQuery(id+"F0.wireOp",EDGE,"E25.5"),sQuery(id+"F0.wireOp",EDGE,"E25.6"),sQuery(id+"F0.wireOp",EDGE,"E25.7")])],"isStart":false});
            var sketch = newSketch(context, id + "F23", { "sketchPlane" : qUnion([Q0])});
            skCircle(sketch, "E98", {"center": v(0, -104.25) * mm, "radius": 6 * mm});
            skSolve(sketch);
        }
        {
            var Q0;
            Q0 = qSketchRegion(id + "F23", true);
            var Q1;
            Q1=makeQuery(id+"F22.opExtrude","CAP_FACE",FACE,{"disambiguationData":[OSD([sQuery(id+"F18.wireOp",EDGE,"E96")])],"isStart":false});
            extrude(context, id + "F24", {"entities" : qUnion([Q0, Q1]), "operationType" : NewBodyOperationType.ADD, "endBound" : BoundingType.THROUGH_ALL, "depth" : 25 * mm});
        }
        {
            var Q0;
            Q0=makeQuery(id+"F24.opExtrude","CAP_FACE",FACE,{"disambiguationData":[OSD([sQuery(id+"F18.wireOp",EDGE,"E96")])],"isStart":false});
            extrude(context, id + "F25", {"entities" : qUnion([Q0]), "operationType" : NewBodyOperationType.ADD, "endBound" : BoundingType.THROUGH_ALL, "depth" : 25 * mm});
        }
    });
